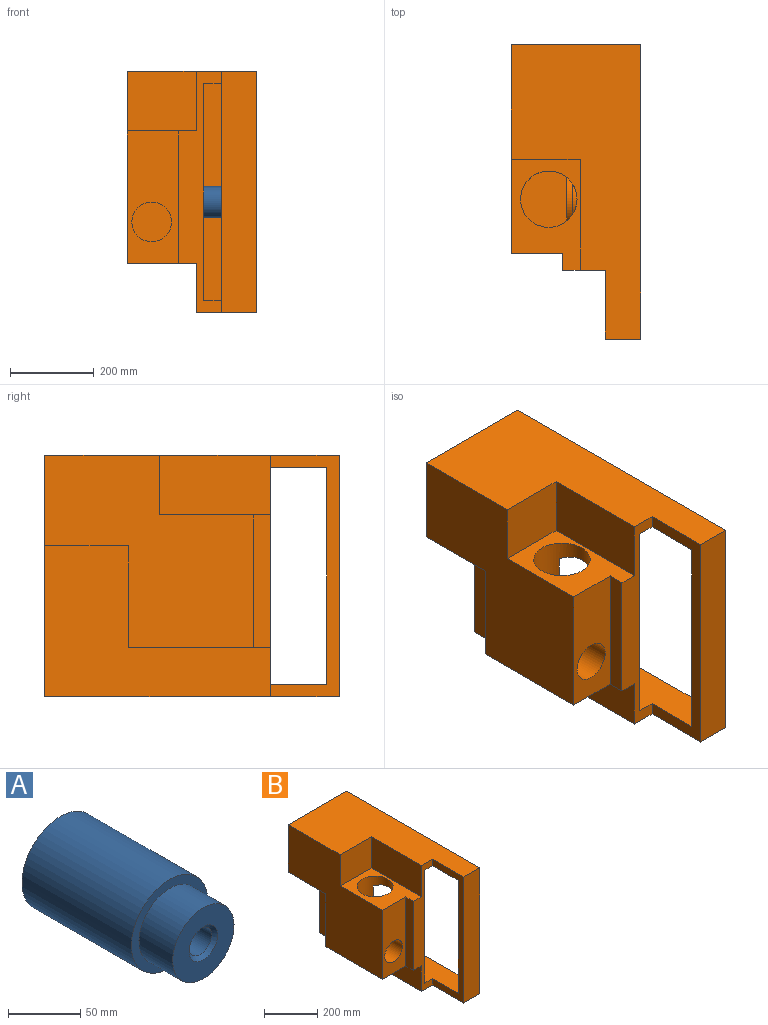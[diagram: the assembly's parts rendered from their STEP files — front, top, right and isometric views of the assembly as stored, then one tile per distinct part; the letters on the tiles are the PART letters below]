
ASSEMBLY  parts=2 mates=1
PART A: 10 faces, bbox 75x140x75 mm
  f0: cylinder r=11mm len=117mm, axis (0,-1,0), area 8086.5mm2, adj f6,f8
  f1: cylinder r=37.5mm len=107mm, axis (0,1,0), area 25211.3mm2, adj f2,f3
  f2: plane 75x75mm, normal (0,-1,0), area 1590.4mm2, adj f1,f4
  f3: plane 75x75mm, normal (0,1,0), area 3161.2mm2, adj f1,f9
  f4: cylinder r=30mm len=60mm, axis (0,1,0), area 6220.4mm2, adj f2,f5
  f5: plane 60x60mm, normal (0,-1,0), area 2211.7mm2, adj f4,f6
  f6: cone r=11mm half-angle=45deg, axis (0,-1,0), area 333.2mm2, adj f0,f5
  f7: cylinder r=17mm len=34mm, axis (0,1,0), area 1815.8mm2, adj f8,f9
  f8: plane 34x34mm, normal (0,1,0), area 527.8mm2, adj f0,f7
  f9: cone r=17mm half-angle=45deg, axis (0,1,0), area 493.2mm2, adj f3,f7
PART B: 42 faces, bbox 310x705x578 mm
  f0: cylinder r=67.5mm len=135mm, axis (0,0,1), area 35142.4mm2, adj f1,f21,f28,f29
  f1: plane 135x110.5mm, normal (0,0,1), area 12541.1mm2, adj f0,f29
  f2: cylinder r=67.5mm len=135mm, axis (0,1,0), area 35142.5mm2, adj f3,f25,f28,f29
  f3: plane 135x110.5mm, normal (0,1,0), area 12541.1mm2, adj f2,f29
  f4: plane 578x310mm, normal (0,1,0), area 119615mm2, adj f8,f10,f14,f15,f20,f24
  f5: plane 578x102mm, normal (0,-1,0), area 26238mm2, adj f6,f8,f10,f11,f12,f13,f18,f19
  f6: plane 317x40mm, normal (-1,0,0), area 12680mm2, adj f5,f7,f19,f21
  f7: plane 317x123mm, normal (0,-1,0), area 31902.8mm2, adj f6,f15,f19,f21,f40
  f8: plane 705x145mm, normal (0,0,-1), area 92325mm2, adj f4,f5,f9,f14,f18,f20
  f9: plane 578x85mm, normal (0,-1,0), area 49130mm2, adj f8,f10,f14,f18
  f10: plane 705x310mm, normal (0,0,1), area 137700mm2, adj f4,f5,f9,f14,f15,f18,f22,f23
  f11: plane 645x127mm, normal (0,0,-1), area 76245mm2, adj f5,f13,f14,f16,f17,f18
  f12: plane 645x127mm, normal (0,0,1), area 76245mm2, adj f5,f13,f14,f16,f17,f18
  f13: plane 518x510mm, normal (1,0,0), area 202604.8mm2, adj f5,f11,f12,f17,f26
  f14: plane 705x578mm, normal (1,0,0), area 73380mm2, adj f4,f8,f9,f10,f11,f12,f16,f17
  f15: plane 500x460mm, normal (-1,0,0), area 149225mm2, adj f4,f7,f10,f19,f21,f23,f24,f25
  f16: plane 518x85mm, normal (0,1,0), area 44030mm2, adj f11,f12,f14,f18
  f17: plane 518x127mm, normal (0,-1,0), area 65786mm2, adj f11,f12,f13,f14
  f18: plane 578x165mm, normal (-1,0,0), area 25440mm2, adj f5,f8,f9,f10,f11,f12,f16
  f19: plane 340x165mm, normal (0,0,-1), area 51180mm2, adj f5,f6,f7,f15,f20,f25
  f20: plane 540x361mm, normal (-1,0,0), area 112320mm2, adj f4,f5,f8,f19,f24,f25
  f21: plane 265x165mm, normal (0,0,1), area 24491.1mm2, adj f0,f5,f6,f7,f15,f22,f23
  f22: plane 265x143mm, normal (-1,0,0), area 37895mm2, adj f5,f10,f21,f23
  f23: plane 165x143mm, normal (0,-1,0), area 23595mm2, adj f10,f15,f21,f22
  f24: plane 200x165mm, normal (0,0,-1), area 33000mm2, adj f4,f15,f20,f25
  f25: plane 243x165mm, normal (0,1,0), area 25781.1mm2, adj f2,f15,f19,f20,f24
  f26: cylinder r=140mm len=280mm, axis (1,0,0), area 14074.3mm2, adj f13,f27
  f27: plane 280x280mm, normal (1,0,0), area 4319.7mm2, adj f26,f28
  f28: cylinder r=135mm len=270mm, axis (1,0,0), area 25235.5mm2, adj f0,f2,f27,f29
  f29: plane 259.57x259.57mm, normal (1,0,0), area 32167.6mm2, adj f0,f1,f2,f3,f28,f30
  f30: cylinder r=62.5mm len=125mm, axis (-1,0,0), area 5301.4mm2, adj f29,f31
  f31: plane 125x125mm, normal (1,0,0), area 1885mm2, adj f30,f32
  f32: cylinder r=57.5mm len=115mm, axis (-1,0,0), area 11199.8mm2, adj f31,f33
  f33: plane 115x115mm, normal (1,0,0), area 4025.2mm2, adj f32,f34
  f34: cylinder r=45mm len=90mm, axis (-1,0,0), area 1131mm2, adj f33,f35
  f35: plane 90x90mm, normal (1,0,0), area 3534.3mm2, adj f34,f36
  f36: cylinder r=30mm len=60mm, axis (1,0,0), area 6785.8mm2, adj f35,f37
  f37: plane 60x60mm, normal (1,0,0), area 2513.3mm2, adj f36,f38
  f38: cylinder r=10mm len=45mm, axis (1,0,0), area 2827.4mm2, adj f37,f39
  f39: plane 20x20mm, normal (1,0,0), area 314.2mm2, adj f38
  f40: cylinder r=47.5mm len=152mm, axis (0,-1,0), area 45364.6mm2, adj f7,f41
  f41: plane 95x95mm, normal (0,-1,0), area 7088.2mm2, adj f40
PLACE A rot(axis=(0.58,0.58,-0.58),120deg) t=(-17.83,-64.22,36.98)mm
PLACE B t=(-306.33,-64.22,36.98)mm fixed
MATE fastened B.f38 <-> A.f0  axis (1,0,0) through (-124.83,-64.22,36.98)mm
